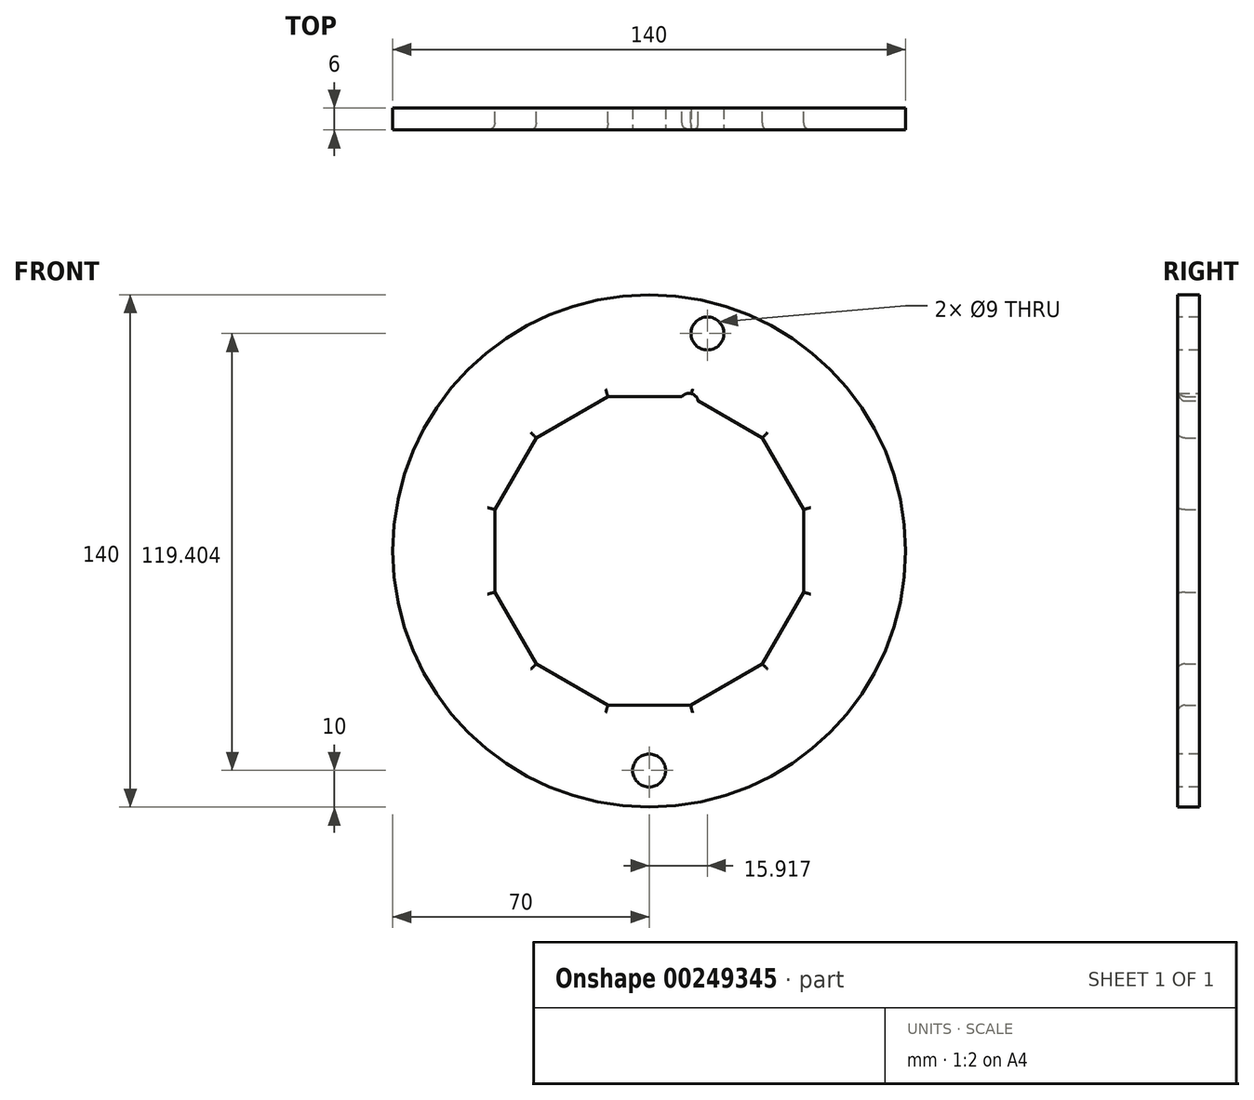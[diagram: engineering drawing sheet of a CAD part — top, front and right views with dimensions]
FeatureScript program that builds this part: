
annotation { "Feature Type Name" : "Feature", "Feature Type Description" : "" }
export const myFeature = defineFeature(function(context is Context, id is Id, definition is map)
    precondition{}
    {
        {
            var Q0;
            Q0=qCreatedBy(makeId("Front.planeOp"),FACE);
            var sketch = newSketch(context, id + "F0", { "sketchPlane" : qUnion([Q0])});
            skCircle(sketch, "E0.cCircle", {"center": v(0, 0) * mm, "radius": 42.15 * mm, "construction": true});
            skLineSegment(sketch, "E0.0", {"start": v(-11.3, 42.15) * mm, "end": v(11.3, 42.15) * mm});
            skLineSegment(sketch, "E0.1", {"start": v(11.3, 42.15) * mm, "end": v(30.86, 30.86) * mm});
            skLineSegment(sketch, "E0.2", {"start": v(30.86, 30.86) * mm, "end": v(42.15, 11.3) * mm});
            skLineSegment(sketch, "E0.3", {"start": v(42.15, 11.3) * mm, "end": v(42.15, -11.3) * mm});
            skLineSegment(sketch, "E0.4", {"start": v(42.15, -11.3) * mm, "end": v(30.86, -30.86) * mm});
            skLineSegment(sketch, "E0.5", {"start": v(30.86, -30.86) * mm, "end": v(11.3, -42.15) * mm});
            skLineSegment(sketch, "E0.6", {"start": v(11.3, -42.15) * mm, "end": v(-11.3, -42.15) * mm});
            skLineSegment(sketch, "E0.7", {"start": v(-11.3, -42.15) * mm, "end": v(-30.86, -30.86) * mm});
            skLineSegment(sketch, "E0.8", {"start": v(-30.86, -30.86) * mm, "end": v(-42.15, -11.3) * mm});
            skLineSegment(sketch, "E0.9", {"start": v(-42.15, -11.3) * mm, "end": v(-42.15, 11.3) * mm});
            skLineSegment(sketch, "E0.10", {"start": v(-42.15, 11.3) * mm, "end": v(-30.86, 30.86) * mm});
            skLineSegment(sketch, "E0.11", {"start": v(-30.86, 30.86) * mm, "end": v(-11.3, 42.15) * mm});
            skPoint(sketch, "E0.0.midPoint", {"position": v(0, 42.15) * mm});
            skCircle(sketch, "E1", {"center": v(0, 0) * mm, "radius": 70 * mm});
            skSolve(sketch);
        }
        {
            var Q0;
            Q0=makeQuery(id+"F0.imprint","IMPRINT",FACE,{"disambiguationData":[TD([[makeQuery(id+"F0.imprint","IMPRINT",EDGE,{"derivedFrom":sQuery(id+"F0.wireOp",EDGE,"E0.0")}),1.0]])]});
            extrude(context, id + "F1", {"entities" : qUnion([Q0]), "depth" : 6 * mm, "symmetric" : true});
        }
        {
            var Q0;
            Q0=qCreatedBy(makeId("Front.planeOp"),FACE);
            var sketch = newSketch(context, id + "F2", { "sketchPlane" : qUnion([Q0])});
            skCircle(sketch, "E2", {"center": v(10.87, 40.57) * mm, "radius": 2.5 * mm});
            skLineSegment(sketch, "E3", {"start": v(10.87, 40.57) * mm, "end": v(0, 0) * mm, "construction": true});
            skSolve(sketch);
        }
        {
            var Q0;
            Q0=makeQuery(id+"F1.opExtrude","CAP_EDGE",EDGE,{"disambiguationData":[OSD([sQuery(id+"F0.wireOp",EDGE,"E0.11")])],"isStart":false});
            var Q1;
            Q1=makeQuery(id+"F1.opExtrude","CAP_EDGE",EDGE,{"disambiguationData":[OSD([sQuery(id+"F0.wireOp",EDGE,"E0.0")])],"isStart":false});
            var Q2;
            Q2=makeQuery(id+"F1.opExtrude","CAP_EDGE",EDGE,{"disambiguationData":[OSD([sQuery(id+"F0.wireOp",EDGE,"E0.1")])],"isStart":false});
            var Q3;
            Q3=makeQuery(id+"F1.opExtrude","CAP_EDGE",EDGE,{"disambiguationData":[OSD([sQuery(id+"F0.wireOp",EDGE,"E0.2")])],"isStart":false});
            var Q4;
            Q4=makeQuery(id+"F1.opExtrude","CAP_EDGE",EDGE,{"disambiguationData":[OSD([sQuery(id+"F0.wireOp",EDGE,"E0.3")])],"isStart":false});
            var Q5;
            Q5=makeQuery(id+"F1.opExtrude","CAP_EDGE",EDGE,{"disambiguationData":[OSD([sQuery(id+"F0.wireOp",EDGE,"E0.4")])],"isStart":false});
            var Q6;
            Q6=makeQuery(id+"F1.opExtrude","CAP_EDGE",EDGE,{"disambiguationData":[OSD([sQuery(id+"F0.wireOp",EDGE,"E0.5")])],"isStart":false});
            var Q7;
            Q7=makeQuery(id+"F1.opExtrude","CAP_EDGE",EDGE,{"disambiguationData":[OSD([sQuery(id+"F0.wireOp",EDGE,"E0.6")])],"isStart":false});
            var Q8;
            Q8=makeQuery(id+"F1.opExtrude","CAP_EDGE",EDGE,{"disambiguationData":[OSD([sQuery(id+"F0.wireOp",EDGE,"E0.7")])],"isStart":false});
            var Q9;
            Q9=makeQuery(id+"F1.opExtrude","CAP_EDGE",EDGE,{"disambiguationData":[OSD([sQuery(id+"F0.wireOp",EDGE,"E0.8")])],"isStart":false});
            var Q10;
            Q10=makeQuery(id+"F1.opExtrude","CAP_EDGE",EDGE,{"disambiguationData":[OSD([sQuery(id+"F0.wireOp",EDGE,"E0.9")])],"isStart":false});
            var Q11;
            Q11=makeQuery(id+"F1.opExtrude","CAP_EDGE",EDGE,{"disambiguationData":[OSD([sQuery(id+"F0.wireOp",EDGE,"E0.10")])],"isStart":false});
            fillet(context, id + "F3", {"entities" : qUnion([Q0, Q1, Q2, Q3, Q4, Q5, Q6, Q7, Q8, Q9, Q10, Q11]), "radius" : 2 * mm, "tangentPropagation" : true, "allowEdgeOverflow" : false});
        }
        {
            var Q0;
            Q0=makeQuery(id+"F2.imprint","IMPRINT",FACE,{"disambiguationData":[TD([[makeQuery(id+"F2.imprint","IMPRINT",EDGE,{"derivedFrom":sQuery(id+"F2.wireOp",EDGE,"E2")}),1.0]])]});
            extrude(context, id + "F4", {"entities" : qUnion([Q0]), "operationType" : NewBodyOperationType.REMOVE, "depth" : 25 * mm, "symmetric" : true});
        }
        {
            var Q0;
            Q0=qCreatedBy(makeId("Front.planeOp"),FACE);
            var sketch = newSketch(context, id + "F5", { "sketchPlane" : qUnion([Q0])});
            skCircle(sketch, "E4", {"center": v(0, -60) * mm, "radius": 4.5 * mm});
            skSolve(sketch);
        }
        {
            var Q0;
            Q0 = qSketchRegion(id + "F5", true);
            extrude(context, id + "F6", {"entities" : qUnion([Q0]), "operationType" : NewBodyOperationType.REMOVE, "oppositeDirection" : true, "depth" : 25 * mm, "symmetric" : true});
        }
        {
            var Q0;
            Q0=qCreatedBy(makeId("Front.planeOp"),FACE);
            var sketch = newSketch(context, id + "F7", { "sketchPlane" : qUnion([Q0])});
            skLineSegment(sketch, "E5", {"start": v(0, 0) * mm, "end": v(15.92, 59.4) * mm, "construction": true});
            skCircle(sketch, "E6", {"center": v(15.92, 59.4) * mm, "radius": 4.5 * mm});
            skSolve(sketch);
        }
        {
            var Q0;
            Q0 = qSketchRegion(id + "F7", true);
            extrude(context, id + "F8", {"entities" : qUnion([Q0]), "operationType" : NewBodyOperationType.REMOVE, "oppositeDirection" : true, "depth" : 25 * mm, "symmetric" : true});
        }
    });
